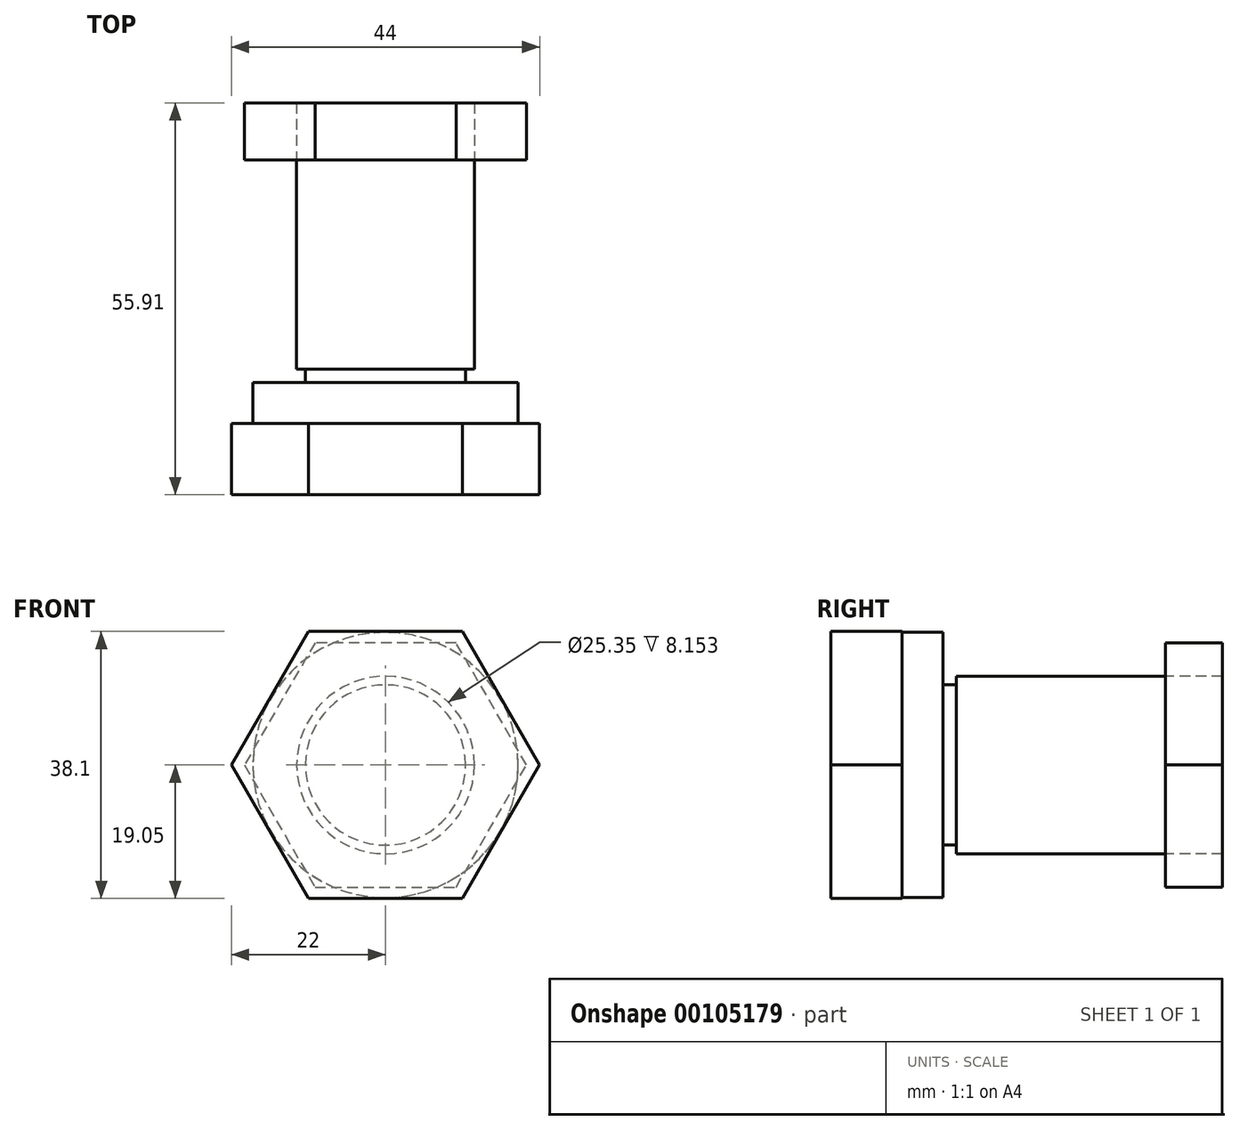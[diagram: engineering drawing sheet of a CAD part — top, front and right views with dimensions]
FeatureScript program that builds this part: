
annotation { "Feature Type Name" : "Feature", "Feature Type Description" : "" }
export const myFeature = defineFeature(function(context is Context, id is Id, definition is map)
    precondition{}
    {
        {
            var Q0;
            Q0=qCreatedBy(makeId("Right.planeOp"),FACE);
            var sketch = newSketch(context, id + "F0", { "sketchPlane" : qUnion([Q0])});
            skLineSegment(sketch, "E0", {"start": v(0, 0) * mm, "end": v(0, 18.92) * mm});
            skLineSegment(sketch, "E1", {"start": v(0, 18.92) * mm, "end": v(16, 18.92) * mm});
            skLineSegment(sketch, "E2", {"start": v(16, 18.92) * mm, "end": v(16, 11.43) * mm});
            skLineSegment(sketch, "E3", {"start": v(47.75, 12.67) * mm, "end": v(47.75, 0) * mm});
            skLineSegment(sketch, "E4", {"start": v(47.75, 0) * mm, "end": v(0, 0) * mm});
            skLineSegment(sketch, "E5", {"start": v(47.75, 12.67) * mm, "end": v(17.9, 12.67) * mm});
            skLineSegment(sketch, "E6", {"start": v(17.9, 12.67) * mm, "end": v(17.9, 11.43) * mm});
            skLineSegment(sketch, "E7", {"start": v(17.9, 11.43) * mm, "end": v(16, 11.43) * mm});
            skSolve(sketch);
        }
        {
            var Q0;
            Q0=makeQuery(id+"F0.imprint","IMPRINT",FACE,{"disambiguationData":[TD([[makeQuery(id+"F0.imprint","IMPRINT",EDGE,{"derivedFrom":sQuery(id+"F0.wireOp",EDGE,"E0")}),-1.0]])]});
            var Q1;
            Q1=sQuery(id+"F0.wireOp",EDGE,"E4");
            revolve(context, id + "F1", {"surfaceOperationType" : NewSurfaceOperationType.NEW, "entities" : qUnion([Q0]), "axis" : qUnion([Q1]), "revolveType" : RevolveType.FULL});
        }
        {
            var Q0;
            Q0=makeQuery(id+"F1.opRevolve","SWEPT_FACE",FACE,{"disambiguationData":[OSD([sQuery(id+"F0.wireOp",EDGE,"E0")])]});
            var sketch = newSketch(context, id + "F2", { "sketchPlane" : qUnion([Q0])});
            skCircle(sketch, "E8.cCircle", {"center": v(0, 0) * mm, "radius": 19.05 * mm, "construction": true});
            skLineSegment(sketch, "E8.0", {"start": v(11, -19.05) * mm, "end": v(-11, -19.05) * mm});
            skLineSegment(sketch, "E8.1", {"start": v(-11, -19.05) * mm, "end": v(-22, 0) * mm});
            skLineSegment(sketch, "E8.2", {"start": v(-22, 0) * mm, "end": v(-11, 19.05) * mm});
            skLineSegment(sketch, "E8.3", {"start": v(-11, 19.05) * mm, "end": v(11, 19.05) * mm});
            skLineSegment(sketch, "E8.4", {"start": v(11, 19.05) * mm, "end": v(22, 0) * mm});
            skLineSegment(sketch, "E8.5", {"start": v(22, 0) * mm, "end": v(11, -19.05) * mm});
            skPoint(sketch, "E8.0.midPoint", {"position": v(0, -19.05) * mm});
            skSolve(sketch);
        }
        {
            var Q0;
            Q0=makeQuery(id+"F2.imprint","IMPRINT",FACE,{"disambiguationData":[TD([[makeQuery(id+"F2.imprint","IMPRINT",EDGE,{"derivedFrom":sQuery(id+"F2.wireOp",EDGE,"E8.0")}),-1.0]])]});
            extrude(context, id + "F3", {"entities" : qUnion([Q0]), "operationType" : NewBodyOperationType.ADD, "oppositeDirection" : true, "depth" : 10.16 * mm, "offsetDistance" : 25.4 * mm});
        }
        {
            var Q0;
            Q0=makeQuery(id+"F1.opRevolve","SWEPT_FACE",FACE,{"disambiguationData":[OSD([sQuery(id+"F0.wireOp",EDGE,"E3")])]});
            var sketch = newSketch(context, id + "F4", { "sketchPlane" : qUnion([Q0])});
            skCircle(sketch, "E9.0.0", {"center": v(0, 0) * mm, "radius": 12.67 * mm});
            skCircle(sketch, "E10.cCircle", {"center": v(0, 0) * mm, "radius": 17.44 * mm, "construction": true});
            skLineSegment(sketch, "E10.0", {"start": v(-10.07, 17.44) * mm, "end": v(10.07, 17.44) * mm});
            skLineSegment(sketch, "E10.1", {"start": v(10.07, 17.44) * mm, "end": v(20.13, 0) * mm});
            skLineSegment(sketch, "E10.2", {"start": v(20.13, 0) * mm, "end": v(10.07, -17.44) * mm});
            skLineSegment(sketch, "E10.3", {"start": v(10.07, -17.44) * mm, "end": v(-10.07, -17.44) * mm});
            skLineSegment(sketch, "E10.4", {"start": v(-10.07, -17.44) * mm, "end": v(-20.13, 0) * mm});
            skLineSegment(sketch, "E10.5", {"start": v(-20.13, 0) * mm, "end": v(-10.07, 17.44) * mm});
            skPoint(sketch, "E10.0.midPoint", {"position": v(0, 17.44) * mm});
            skSolve(sketch);
        }
        {
            var Q0;
            Q0=makeQuery(id+"F4.imprint","IMPRINT",FACE,{"disambiguationData":[TD([[makeQuery(id+"F4.imprint","IMPRINT",EDGE,{"derivedFrom":sQuery(id+"F4.wireOp",EDGE,"E9.0.0")}),-1.0]])]});
            extrude(context, id + "F5", {"entities" : qUnion([Q0]), "depth" : 8.15 * mm, "offsetDistance" : 25.4 * mm});
        }
    });
